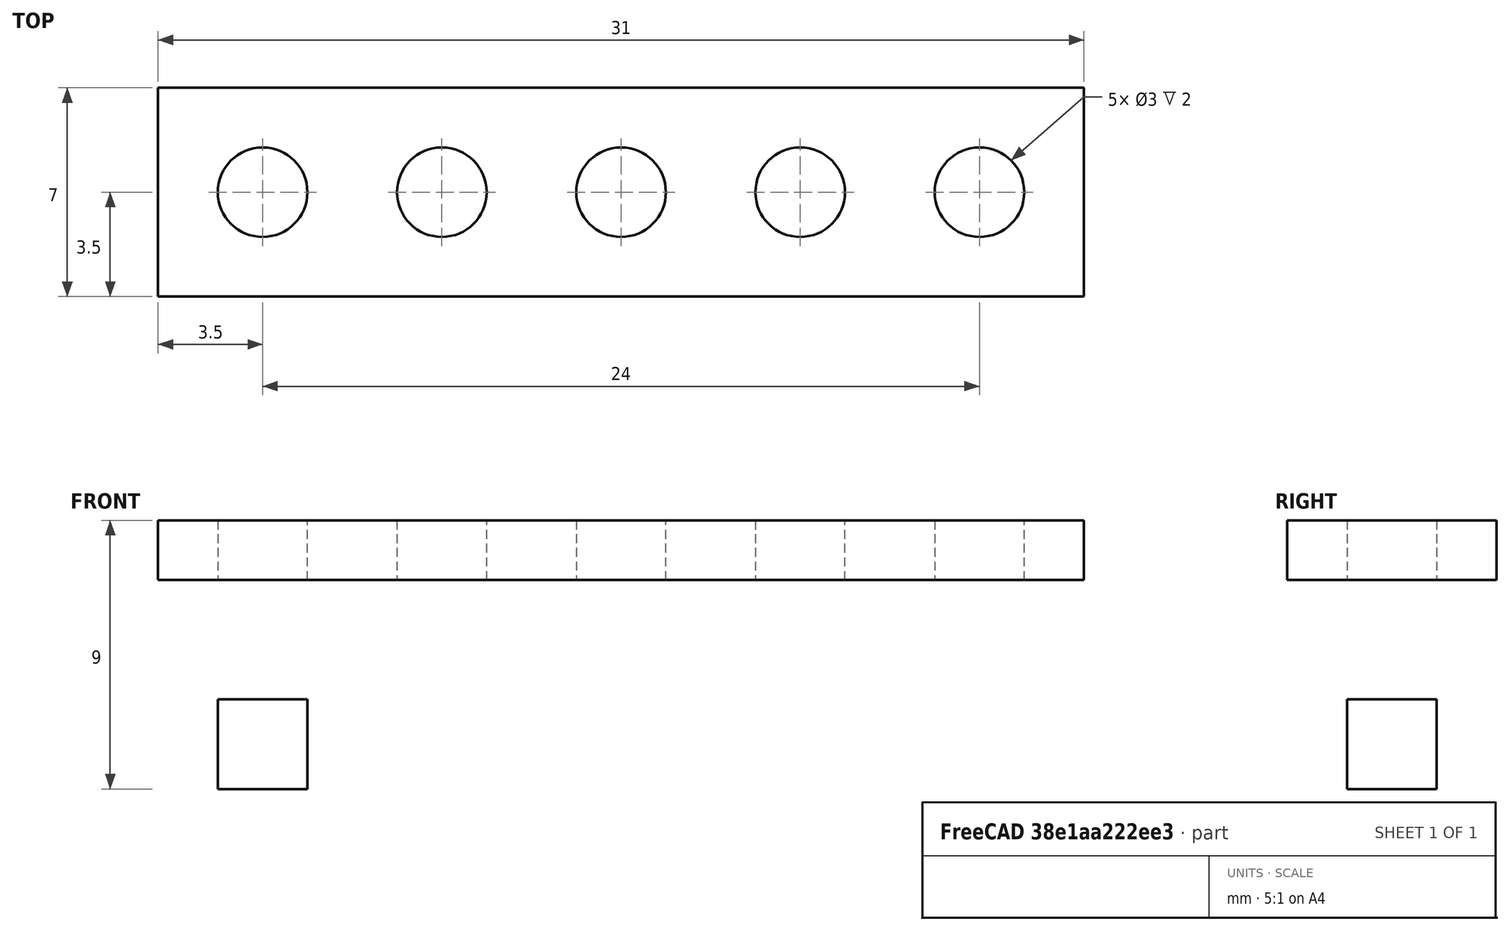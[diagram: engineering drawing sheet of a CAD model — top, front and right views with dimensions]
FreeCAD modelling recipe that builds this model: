
FCSTD DOCUMENT  (FreeCAD 0.21R33694 (Git))
Label: OJT1_T10P02.error
License: All rights reserved
LicenseURL: http://en.wikipedia.org/wiki/All_rights_reserved
objects: Part::Box×1, Part::Cylinder×1, Part::FeaturePython×1, Part::Cut×1
note: 3 computed .brp shape members not serialized (recipe doc carries the construction recipe); baked Part::Feature solids carry a one-line shape summary decoded from their .brp

FEATURE [Part::Box] Box  label="Cub"
  AttacherType = Attacher::AttachEngine3D
  Height = 2
  Length = 31
  Width = 7
FEATURE [Part::Cylinder] Cylinder  label="Cilindre"
  Angle = 360
  AttacherType = Attacher::AttachEngine3D
  FirstAngle = 0
  Height = 3
  Placement = pos=(3.5,3.5,-7) rot=(0,0,1;0rad)
  Radius = 1.5
  SecondAngle = 0
FEATURE [Part::FeaturePython] Array  # Draft array (typed FeaturePython)
  AlwaysSyncPlacement = false
  Angle = 360
  ArrayType = 0
  Axis = (0,0,1)
  Base = -> Cylinder
  Center = (0,0,0)
  Count = 5
  ExpandArray = false
  Fuse = false
  IntervalAxis = (0,0,0)
  IntervalX = (6,0,0)
  IntervalY = (0,100,0)
  IntervalZ = (0,0,100)
  NumberCircles = 3
  NumberPolar = 5
  NumberX = 5
  NumberY = 1
  NumberZ = 1
  Placement = pos=(0,-8.34465e-07,7) rot=(0,0,1;0rad)
  PlacementList = 5 placements: arithmetic series from (3.5,3.5,-7) step (6,0,0) to (27.5,3.5,-7)
  RadialDistance = 50
  ScaleList = (5) [(1,1,1),(1,1,1),(1,1,1),(1,1,1),(1,1,1)]
  Symmetry = 1
  TangentialDistance = 25
FEATURE [Part::Cut] Cut
  Base = -> Box
  Refine = true
  Tool = -> Array
